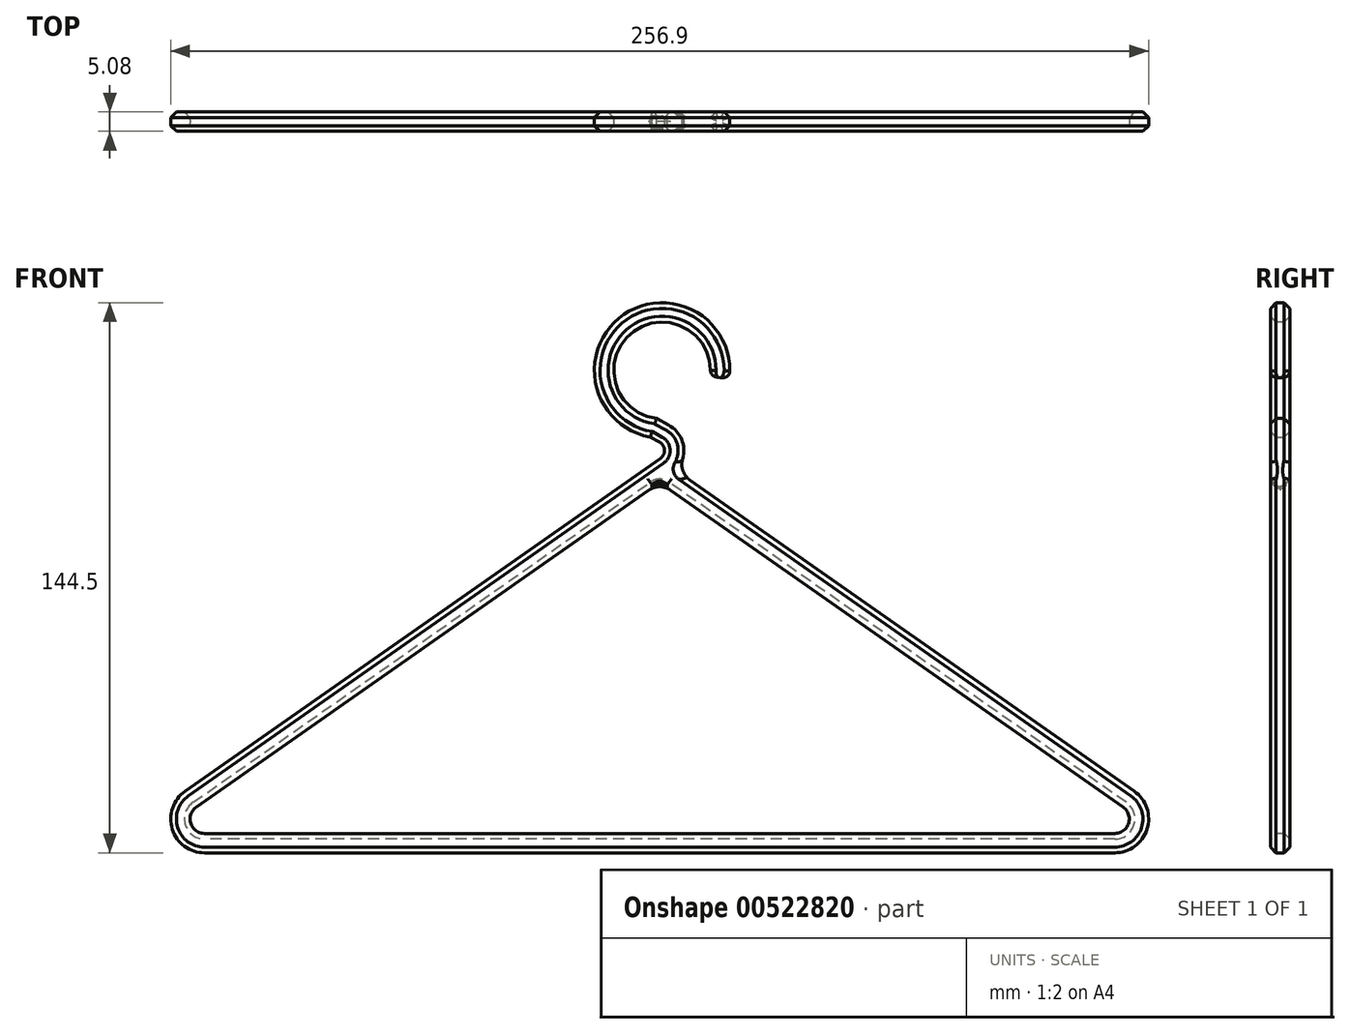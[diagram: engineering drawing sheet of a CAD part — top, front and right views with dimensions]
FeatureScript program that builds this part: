
annotation { "Feature Type Name" : "Feature", "Feature Type Description" : "" }
export const myFeature = defineFeature(function(context is Context, id is Id, definition is map)
    precondition{}
    {
        {
            var Q0;
            Q0=qCreatedBy(makeId("Front.planeOp"),FACE);
            var sketch = newSketch(context, id + "F0", { "sketchPlane" : qUnion([Q0])});
            skLineSegment(sketch, "E0", {"start": v(0, 0) * mm, "end": v(-119.56, 0) * mm});
            skLineSegment(sketch, "E1", {"start": v(-123.2, 11.55) * mm, "end": v(1.64, 98.96) * mm});
            skArc(sketch, "E2", {"start": v(15.77, 122.33) * mm, "mid": v(-8.58, 136.3) * mm, "end": v(-1.63, 109.1) * mm});
            skPoint(sketch, "E2.second.point", {"position": v(0.53, 139.42) * mm});
            skPoint(sketch, "E3.visualSharp", {"position": v(-139.7, 0) * mm});
            skArc(sketch, "E3.filletArc", {"start": v(-123.2, 11.55) * mm, "mid": v(-125.62, 4.44) * mm, "end": v(-119.56, 0) * mm});
            skLineSegment(sketch, "E4", {"start": v(-1.63, 109.1) * mm, "end": v(1.16, 107.58) * mm});
            skPoint(sketch, "E5.visualSharp", {"position": v(8.34, 103.66) * mm});
            skArc(sketch, "E5.filletArc", {"start": v(1.64, 98.96) * mm, "mid": v(3.8, 103.4) * mm, "end": v(1.16, 107.58) * mm});
            skLineSegment(sketch, "E6", {"start": v(0, 0) * mm, "end": v(119.56, 0) * mm});
            skLineSegment(sketch, "E7", {"start": v(123.2, 11.55) * mm, "end": v(0, 97.82) * mm});
            skPoint(sketch, "E8.visualSharp", {"position": v(139.7, 0) * mm});
            skArc(sketch, "E8.filletArc", {"start": v(119.56, 0) * mm, "mid": v(125.62, 4.44) * mm, "end": v(123.2, 11.55) * mm});
            skSolve(sketch);
        }
        {
            var Q0;
            Q0=qCreatedBy(makeId("Right.planeOp"),FACE);
            var sketch = newSketch(context, id + "F1", { "sketchPlane" : qUnion([Q0])});
            skCircle(sketch, "E9.cCircle", {"center": v(0, 0) * mm, "radius": 2.54 * mm, "construction": true});
            skLineSegment(sketch, "E9.0", {"start": v(-1.05, 2.54) * mm, "end": v(1.05, 2.54) * mm});
            skLineSegment(sketch, "E9.1", {"start": v(1.05, 2.54) * mm, "end": v(2.54, 1.05) * mm});
            skLineSegment(sketch, "E9.2", {"start": v(2.54, 1.05) * mm, "end": v(2.54, -1.05) * mm});
            skLineSegment(sketch, "E9.3", {"start": v(2.54, -1.05) * mm, "end": v(1.05, -2.54) * mm});
            skLineSegment(sketch, "E9.4", {"start": v(1.05, -2.54) * mm, "end": v(-1.05, -2.54) * mm});
            skLineSegment(sketch, "E9.5", {"start": v(-1.05, -2.54) * mm, "end": v(-2.54, -1.05) * mm});
            skLineSegment(sketch, "E9.6", {"start": v(-2.54, -1.05) * mm, "end": v(-2.54, 1.05) * mm});
            skLineSegment(sketch, "E9.7", {"start": v(-2.54, 1.05) * mm, "end": v(-1.05, 2.54) * mm});
            skPoint(sketch, "E9.0.midPoint", {"position": v(0, 2.54) * mm});
            skSolve(sketch);
        }
        {
            var Q0;
            Q0=makeQuery(id+"F1.imprint","IMPRINT",FACE,{"disambiguationData":[TD([[makeQuery(id+"F1.imprint","IMPRINT",EDGE,{"derivedFrom":sQuery(id+"F1.wireOp",EDGE,"E9.0")}),-1.0]])]});
            var Q1;
            Q1=sQuery(id+"F0.wireOp",EDGE,"E0");
            var Q2;
            Q2=sQuery(id+"F0.wireOp",EDGE,"E1");
            var Q3;
            Q3=sQuery(id+"F0.wireOp",EDGE,"E3.filletArc");
            var Q4;
            Q4=sQuery(id+"F0.wireOp",EDGE,"E5.filletArc");
            var Q5;
            Q5=sQuery(id+"F0.wireOp",EDGE,"E4");
            var Q6;
            Q6=sQuery(id+"F0.wireOp",EDGE,"E2");
            sweep(context, id + "F2", {"profiles" : qUnion([Q0]), "path" : qUnion([Q1, Q2, Q3, Q4, Q5, Q6])});
        }
        {
            var Q0;
            Q0=makeQuery(id+"F2.opSweep","SWEPT_BODY",BODY,{"disambiguationData":[OSD([sQuery(id+"F0.wireOp",EDGE,"E0"),sQuery(id+"F1.wireOp",EDGE,"E9.0"),sQuery(id+"F1.wireOp",EDGE,"E9.1"),sQuery(id+"F1.wireOp",EDGE,"E9.2"),sQuery(id+"F1.wireOp",EDGE,"E9.3"),sQuery(id+"F1.wireOp",EDGE,"E9.4"),sQuery(id+"F1.wireOp",EDGE,"E9.5"),sQuery(id+"F1.wireOp",EDGE,"E9.6"),sQuery(id+"F1.wireOp",EDGE,"E9.7")])]});
            var Q1;
            Q1=qCreatedBy(makeId("Front.planeOp"),FACE);
            mirror(context, id + "F3", {"operationType" : NewBodyOperationType.ADD, "entities" : qUnion([Q0]), "mirrorPlane" : qUnion([Q1])});
        }
        {
            var Q0;
            Q0=qSketchRegion(id+"F1",true);
            var Q1;
            Q1=sQuery(id+"F0.wireOp",EDGE,"E6");
            var Q2;
            Q2=sQuery(id+"F0.wireOp",EDGE,"E7");
            var Q3;
            Q3=sQuery(id+"F0.wireOp",EDGE,"E8.filletArc");
            sweep(context, id + "F4", {"operationType" : NewBodyOperationType.ADD, "profiles" : qUnion([Q0]), "path" : qUnion([Q1, Q2, Q3])});
        }
        {
            var Q0;
            Q0=makeQuery(id+"F4.boolean.opBoolean","INTERSECT",EDGE,{"derivedFrom":[makeQuery(id+"F2.opSweep","SWEPT_FACE",FACE,{"disambiguationData":[OSD([sQuery(id+"F0.wireOp",EDGE,"E5.filletArc"),sQuery(id+"F1.wireOp",EDGE,"E9.7")])]}),makeQuery(id+"F4.opSweep","SWEPT_FACE",FACE,{"disambiguationData":[OSD([sQuery(id+"F0.wireOp",EDGE,"E7"),sQuery(id+"F1.wireOp",EDGE,"E9.5")])]})]});
            var Q1;
            Q1=makeQuery(id+"F4.boolean.opBoolean","INTERSECT",EDGE,{"derivedFrom":[makeQuery(id+"F2.opSweep","SWEPT_FACE",FACE,{"disambiguationData":[OSD([sQuery(id+"F0.wireOp",EDGE,"E5.filletArc"),sQuery(id+"F1.wireOp",EDGE,"E9.0")])]}),makeQuery(id+"F4.opSweep","SWEPT_FACE",FACE,{"disambiguationData":[OSD([sQuery(id+"F0.wireOp",EDGE,"E7"),sQuery(id+"F1.wireOp",EDGE,"E9.4")])]})]});
            var Q2;
            Q2=makeQuery(id+"F4.boolean.opBoolean","INTERSECT",EDGE,{"derivedFrom":[makeQuery(id+"F2.opSweep","SWEPT_FACE",FACE,{"disambiguationData":[OSD([sQuery(id+"F0.wireOp",EDGE,"E5.filletArc"),sQuery(id+"F1.wireOp",EDGE,"E9.1")])]}),makeQuery(id+"F4.opSweep","SWEPT_FACE",FACE,{"disambiguationData":[OSD([sQuery(id+"F0.wireOp",EDGE,"E7"),sQuery(id+"F1.wireOp",EDGE,"E9.3")])]})]});
            var Q3;
            {var subQ0=sQuery(id+"F1.wireOp",EDGE,"E9.0");Q3=makeQuery(id+"F4.boolean.opBoolean","INTERSECT",EDGE,{"derivedFrom":[makeQuery(id+"F2.opSweep","SWEPT_FACE",FACE,{"disambiguationData":[OSD([sQuery(id+"F0.wireOp",EDGE,"E1"),subQ0])]}),makeQuery(id+"F4.opSweep","SWEPT_FACE",FACE,{"disambiguationData":[OSD([sQuery(id+"F0.wireOp",EDGE,"E7"),subQ0])]})]});}
            var Q4;
            {var subQ0=sQuery(id+"F1.wireOp",EDGE,"E9.7");Q4=makeQuery(id+"F4.boolean.opBoolean","INTERSECT",EDGE,{"derivedFrom":[makeQuery(id+"F2.opSweep","SWEPT_FACE",FACE,{"disambiguationData":[OSD([sQuery(id+"F0.wireOp",EDGE,"E1"),subQ0])]}),makeQuery(id+"F4.opSweep","SWEPT_FACE",FACE,{"disambiguationData":[OSD([sQuery(id+"F0.wireOp",EDGE,"E7"),subQ0])]})]});}
            var Q5;
            {var subQ0=sQuery(id+"F1.wireOp",EDGE,"E9.1");Q5=makeQuery(id+"F4.boolean.opBoolean","INTERSECT",EDGE,{"derivedFrom":[makeQuery(id+"F2.opSweep","SWEPT_FACE",FACE,{"disambiguationData":[OSD([sQuery(id+"F0.wireOp",EDGE,"E1"),subQ0])]}),makeQuery(id+"F4.opSweep","SWEPT_FACE",FACE,{"disambiguationData":[OSD([sQuery(id+"F0.wireOp",EDGE,"E7"),subQ0])]})]});}
            fillet(context, id + "F5", {"entities" : qUnion([Q0, Q1, Q2, Q3, Q4, Q5]), "radius" : 5.08 * mm, "tangentPropagation" : true, "allowEdgeOverflow" : false});
        }
        {
            var Q0;
            {var subQ0=sQuery(id+"F1.wireOp",EDGE,"E9.7");var subQ1=sQuery(id+"F1.wireOp",EDGE,"E9.0");Q0=makeQuery(id+"F4.boolean.opBoolean","MERGE",EDGE,{"derivedFrom":[makeQuery(id+"F2.opSweep","SWEPT_EDGE",EDGE,{"disambiguationData":[OSD([sQuery(id+"F0.wireOp",EDGE,"E0"),subQ1,subQ0])]}),makeQuery(id+"F4.opSweep","SWEPT_EDGE",EDGE,{"disambiguationData":[OSD([sQuery(id+"F0.wireOp",EDGE,"E6"),subQ1,subQ0])]})]});}
            var Q1;
            {var subQ0=sQuery(id+"F1.wireOp",EDGE,"E9.7");var subQ1=sQuery(id+"F1.wireOp",EDGE,"E9.6");Q1=makeQuery(id+"F4.boolean.opBoolean","MERGE",EDGE,{"derivedFrom":[makeQuery(id+"F2.opSweep","SWEPT_EDGE",EDGE,{"disambiguationData":[OSD([sQuery(id+"F0.wireOp",EDGE,"E0"),subQ1,subQ0])]}),makeQuery(id+"F4.opSweep","SWEPT_EDGE",EDGE,{"disambiguationData":[OSD([sQuery(id+"F0.wireOp",EDGE,"E6"),subQ1,subQ0])]})]});}
            var Q2;
            {var subQ0=sQuery(id+"F1.wireOp",EDGE,"E9.1");var subQ1=sQuery(id+"F1.wireOp",EDGE,"E9.0");Q2=makeQuery(id+"F4.boolean.opBoolean","MERGE",EDGE,{"derivedFrom":[makeQuery(id+"F2.opSweep","SWEPT_EDGE",EDGE,{"disambiguationData":[OSD([sQuery(id+"F0.wireOp",EDGE,"E0"),subQ1,subQ0])]}),makeQuery(id+"F4.opSweep","SWEPT_EDGE",EDGE,{"disambiguationData":[OSD([sQuery(id+"F0.wireOp",EDGE,"E6"),subQ1,subQ0])]})]});}
            fillet(context, id + "F6", {"entities" : qUnion([Q0, Q1, Q2]), "radius" : 2.54 * mm, "tangentPropagation" : true, "allowEdgeOverflow" : false});
        }
        {
            var Q0;
            Q0=makeQuery(id+"F2.opSweep","CAP_EDGE",EDGE,{"disambiguationData":[OSD([sQuery(id+"F0.wireOp",VERTEX,"E2.start"),sQuery(id+"F1.wireOp",EDGE,"E9.7")])],"isStart":false});
            var Q1;
            Q1=makeQuery(id+"F2.opSweep","CAP_EDGE",EDGE,{"disambiguationData":[OSD([sQuery(id+"F0.wireOp",VERTEX,"E2.start"),sQuery(id+"F1.wireOp",EDGE,"E9.3")])],"isStart":false});
            var Q2;
            Q2=makeQuery(id+"F2.opSweep","CAP_EDGE",EDGE,{"disambiguationData":[OSD([sQuery(id+"F0.wireOp",VERTEX,"E2.start"),sQuery(id+"F1.wireOp",EDGE,"E9.5")])],"isStart":false});
            var Q3;
            Q3=makeQuery(id+"F2.opSweep","CAP_EDGE",EDGE,{"disambiguationData":[OSD([sQuery(id+"F0.wireOp",VERTEX,"E2.start"),sQuery(id+"F1.wireOp",EDGE,"E9.4")])],"isStart":false});
            var Q4;
            Q4=makeQuery(id+"F2.opSweep","CAP_EDGE",EDGE,{"disambiguationData":[OSD([sQuery(id+"F0.wireOp",VERTEX,"E2.start"),sQuery(id+"F1.wireOp",EDGE,"E9.0")])],"isStart":false});
            var Q5;
            Q5=makeQuery(id+"F2.opSweep","CAP_EDGE",EDGE,{"disambiguationData":[OSD([sQuery(id+"F0.wireOp",VERTEX,"E2.start"),sQuery(id+"F1.wireOp",EDGE,"E9.1")])],"isStart":false});
            var Q6;
            Q6=makeQuery(id+"F2.opSweep","CAP_EDGE",EDGE,{"disambiguationData":[OSD([sQuery(id+"F0.wireOp",VERTEX,"E2.start"),sQuery(id+"F1.wireOp",EDGE,"E9.2")])],"isStart":false});
            var Q7;
            Q7=makeQuery(id+"F2.opSweep","CAP_EDGE",EDGE,{"disambiguationData":[OSD([sQuery(id+"F0.wireOp",VERTEX,"E2.start"),sQuery(id+"F1.wireOp",EDGE,"E9.6")])],"isStart":false});
            fillet(context, id + "F7", {"entities" : qUnion([Q0, Q1, Q2, Q3, Q4, Q5, Q6, Q7]), "radius" : 1.78 * mm, "tangentPropagation" : true, "allowEdgeOverflow" : false});
        }
    });
